# Revit family: Lighting_Fixture-Wall-Astro-Goya UPDATEDxxxxxx
name_source: partatom
category: Lighting Fixtures
revit_build: Autodesk Revit LT 2014 (Build: 20130308_1515(x64)
units: mm (PartAtom-declared; Revit-internal decimal feet)

## types (10) — shared parameters
Assembly Code = D5020200
Class = 1
Description = Picture Light
Dimmable = No
Height = 52 mm
IP Rating = IP20
Lamp included = Yes
Light Source From Wall = 350 mm  [stored 1.14829 ft]
Manufacturer = Astro Lighting Ltd, CM20 2DP
Mountable on normally flammable surfaces = Yes
Number of Poles = 1
Product Documentation = http://www.astrolighting.co.uk
Rotation Point A Length = 15 mm  [stored 0.0492126 ft]
Rotation Point B Length = 40 mm
Suitable for bathroom zone = Zone 3
URL = www.astrolighting.co.uk
Voltage = 230 V

## per-type parameters (varying)
| type | Apparent Load | Arm Length | Casing Material | Energy Efficiency Rating | Lamp | Lamp Head Inner Radius | Lamp Head Radius | Lamp Head Reference Line Length | Length | Luminaire Lamp Efficiency Rating | Model | Type Comments | Void Length | Void Placement | Void Radius | Wattage Comments | Weight | Width | ies file |
| 0528 Goya 365 (Brushed Nickel) | 8 VA | 150 mm  [stored 0.492126 ft] | Astro - Steel - Brushed Nickel | - A | T5 | 15.25 mm  [stored 0.0500328 ft] | 16.25 mm  [stored 0.0533136 ft] | 24.3 mm  [stored 0.0797244 ft] | 208.25 mm  [stored 0.683235 ft] | A* -A | 0528 Goya 365 Brushed Nickel | Not suitable for frequent switching. Includes integral electronic ballast. | 305 mm  [stored 1.00066 ft] | 17.5 mm  [stored 0.0574147 ft] | 12.5 mm  [stored 0.0410105 ft] | 8w | 1kg | 362 mm  [stored 1.18766 ft] | Lighting_Fixture-Astro-Goya-ies : ies file - 0528 Goya 365 |
| 0529 Goya 590 (Brushed Nickel) | 14 VA | 150 mm  [stored 0.492126 ft] | Astro - Steel - Brushed Nickel | - A | T5 | 15.25 mm  [stored 0.0500328 ft] | 16.25 mm  [stored 0.0533136 ft] | 24.3 mm  [stored 0.0797244 ft] | 208.25 mm  [stored 0.683235 ft] | A* -A | 0529 Goya 590 Brushed Nickel | Not suitable for frequent switching. Includes integral electronic ballast. | 535 mm  [stored 1.75525 ft] | 17.5 mm  [stored 0.0574147 ft] | 12.5 mm  [stored 0.0410105 ft] | 13w | 1.2kg | 590 mm  [stored 1.9357 ft] | Lighting_Fixture-Astro-Goya-ies : ies file - 0529 Goya 590 |
| 0873 Goya 460 (Brushed Nickel) | 7 VA | 156 mm  [stored 0.511811 ft] | Astro - Steel - Brushed Nickel |  | LED | 10 mm  [stored 0.0328084 ft] | 11 mm  [stored 0.0360892 ft] | 19.05 mm  [stored 0.0625 ft] | 209 mm  [stored 0.685696 ft] | A | 0873 Goya 460 Brushed Nickel | Includes integral LED driver. | 410 mm  [stored 1.34514 ft] | 19 mm  [stored 0.062336 ft] | 13 mm | 5w | 0.9kg | 460 mm  [stored 1.50919 ft] | Lighting_Fixture-Astro-Goya-ies : ies file - 0873 Goya 460 |
| 0875 Goya 760 (Brushed Nickel) | 10 VA | 156 mm  [stored 0.511811 ft] | Astro - Steel - Brushed Nickel |  | LED | 10 mm  [stored 0.0328084 ft] | 11 mm  [stored 0.0360892 ft] | 19.05 mm  [stored 0.0625 ft] | 209 mm  [stored 0.685696 ft] | A | 0875 Goya 760 Brushed Nickel | Includes integral LED driver. | 705 mm  [stored 2.31299 ft] | 19 mm  [stored 0.062336 ft] | 13 mm | 8w | 1.3kg | 760 mm | Lighting_Fixture-Astro-Goya-ies : ies file - 0875 Goya 760 |
| 0534 Goya 365 (Antique Brass) | 8 VA | 150 mm  [stored 0.492126 ft] | Astro - Steel - Antique Brass | - A | T5 | 15.25 mm  [stored 0.0500328 ft] | 16.25 mm  [stored 0.0533136 ft] | 24.3 mm  [stored 0.0797244 ft] | 208.25 mm  [stored 0.683235 ft] | A* -A | 0534 Goya 365 Antique Brass | Not suitable for frequent switching. Includes integral electronic ballast. | 305 mm  [stored 1.00066 ft] | 17.5 mm  [stored 0.0574147 ft] | 12.5 mm  [stored 0.0410105 ft] | 8w | 1kg | 362 mm  [stored 1.18766 ft] | Lighting_Fixture-Astro-Goya-ies : ies file - 0528 Goya 365 |
| 0700 Goya 365 (Chrome) | 8 VA | 150 mm  [stored 0.492126 ft] | Astro - Steel - Chrome Finish | - A | T5 | 15.25 mm  [stored 0.0500328 ft] | 16.25 mm  [stored 0.0533136 ft] | 24.3 mm  [stored 0.0797244 ft] | 208.25 mm  [stored 0.683235 ft] | A* -A | 0700 Goya 365 Chrome | Not suitable for frequent switching. Includes integral electronic ballast. | 305 mm  [stored 1.00066 ft] | 17.5 mm  [stored 0.0574147 ft] | 12.5 mm  [stored 0.0410105 ft] | 8w | 1kg | 362 mm  [stored 1.18766 ft] | Lighting_Fixture-Astro-Goya-ies : ies file - 0528 Goya 365 |
| 0535 Goya 590 (Antique Brass) | 14 VA | 150 mm  [stored 0.492126 ft] | Astro - Steel - Antique Brass | - A | T5 | 15.25 mm  [stored 0.0500328 ft] | 16.25 mm  [stored 0.0533136 ft] | 24.3 mm  [stored 0.0797244 ft] | 208.25 mm  [stored 0.683235 ft] | A* -A | 0535 Goya 590 Antique Brass | Not suitable for frequent switching. Includes integral electronic ballast. | 535 mm  [stored 1.75525 ft] | 17.5 mm  [stored 0.0574147 ft] | 12.5 mm  [stored 0.0410105 ft] | 13w | 1.2kg | 590 mm  [stored 1.9357 ft] | Lighting_Fixture-Astro-Goya-ies : ies file - 0529 Goya 590 |
| 0701 Goya 590 (Chrome) | 14 VA | 150 mm  [stored 0.492126 ft] | Astro - Steel - Chrome Finish | - A | T5 | 15.25 mm  [stored 0.0500328 ft] | 16.25 mm  [stored 0.0533136 ft] | 24.3 mm  [stored 0.0797244 ft] | 208.25 mm  [stored 0.683235 ft] | A* -A | 0701 Goya 590 Chrome | Not suitable for frequent switching. Includes integral electronic ballast. | 535 mm  [stored 1.75525 ft] | 17.5 mm  [stored 0.0574147 ft] | 12.5 mm  [stored 0.0410105 ft] | 13w | 1.2kg | 590 mm  [stored 1.9357 ft] | Lighting_Fixture-Astro-Goya-ies : ies file - 0529 Goya 590 |
| 0874 Goya 460 (Chrome) | 7 VA | 156 mm  [stored 0.511811 ft] | Astro - Steel - Chrome Finish |  | LED | 10 mm  [stored 0.0328084 ft] | 11 mm  [stored 0.0360892 ft] | 19.05 mm  [stored 0.0625 ft] | 209 mm  [stored 0.685696 ft] | A | 0874 Goya 460 Chrome | Includes integral LED driver. | 410 mm  [stored 1.34514 ft] | 19 mm  [stored 0.062336 ft] | 13 mm | 5w | 0.9kg | 460 mm  [stored 1.50919 ft] | Lighting_Fixture-Astro-Goya-ies : ies file - 0873 Goya 460 |
| 0876 Goya 760 (Chrome) | 10 VA | 156 mm  [stored 0.511811 ft] | Astro - Steel - Chrome Finish |  | LED | 10 mm  [stored 0.0328084 ft] | 11 mm  [stored 0.0360892 ft] | 19.05 mm  [stored 0.0625 ft] | 209 mm  [stored 0.685696 ft] | A | 0876 Goya 760 Chrome | Includes integral LED driver. | 705 mm  [stored 2.31299 ft] | 19 mm  [stored 0.062336 ft] | 13 mm | 8w | 1.3kg | 760 mm | Lighting_Fixture-Astro-Goya-ies : ies file - 0875 Goya 760 |

note: [stored X ft] marks values corroborated as IEEE doubles in the binary element streams (Revit-internal decimal feet)

## geometry (parser evidence)
native form markers: Blend x2, Sweep x2
no freeform markers — native parametric forms only
